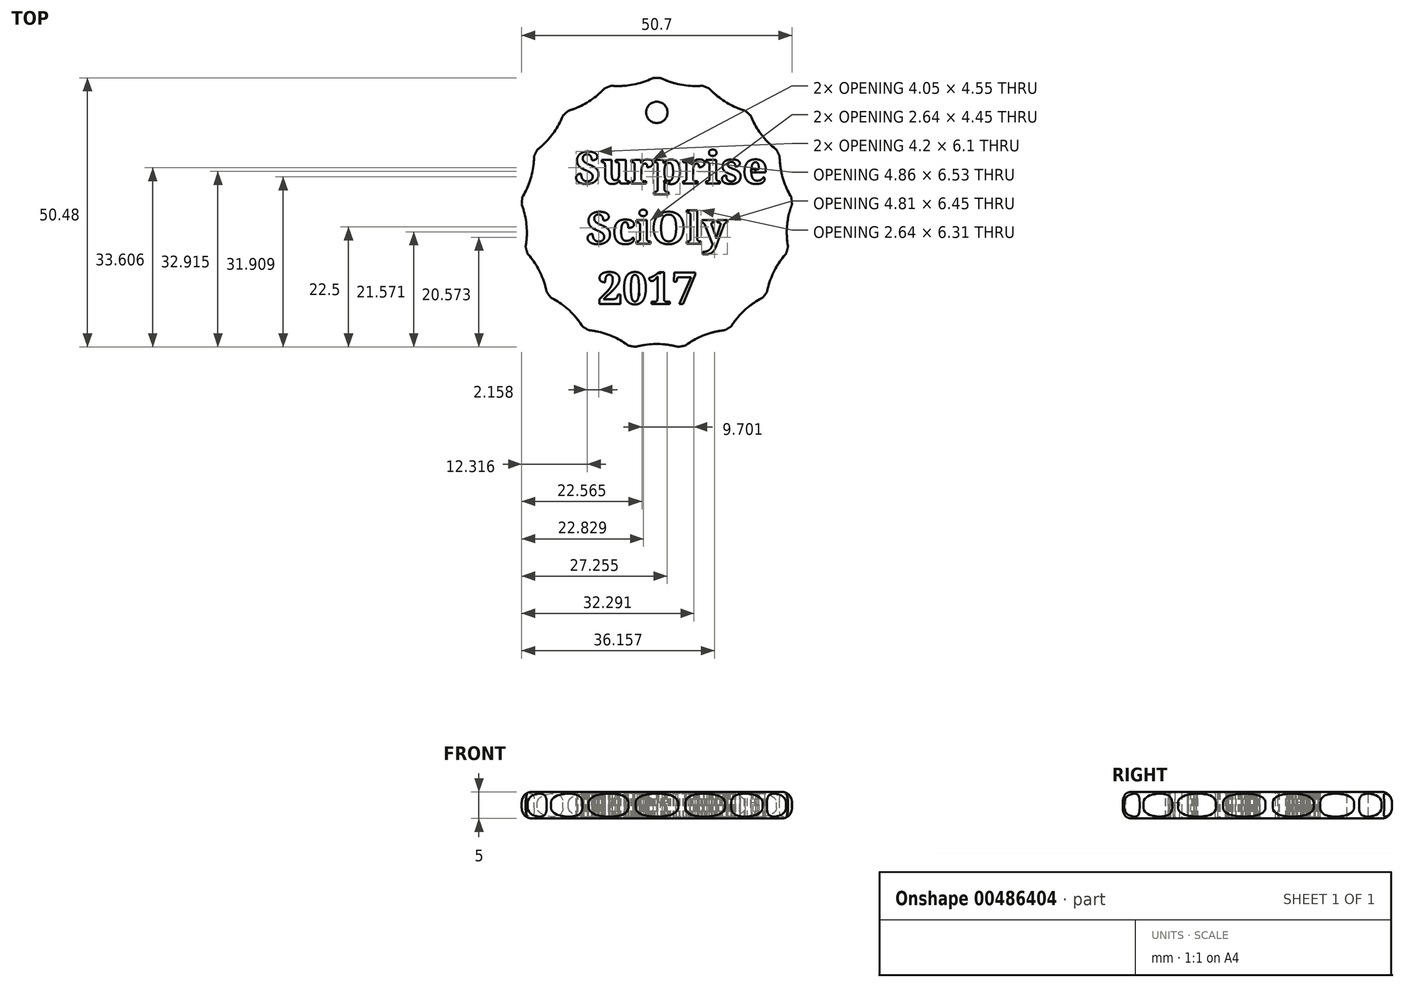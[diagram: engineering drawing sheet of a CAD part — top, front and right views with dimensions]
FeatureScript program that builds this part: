
annotation { "Feature Type Name" : "Feature", "Feature Type Description" : "" }
export const myFeature = defineFeature(function(context is Context, id is Id, definition is map)
    precondition{}
    {
        {
            var Q0;
            Q0=qCreatedBy(makeId("Top.planeOp"),FACE);
            var sketch = newSketch(context, id + "F0", { "sketchPlane" : qUnion([Q0])});
            skCircle(sketch, "E0", {"center": v(0, 0) * mm, "radius": 25.4 * mm});
            skSolve(sketch);
        }
        {
            var Q0;
            Q0=makeQuery(id+"F0.imprint","IMPRINT",FACE,{"disambiguationData":[TD([[makeQuery(id+"F0.imprint","IMPRINT",EDGE,{"derivedFrom":sQuery(id+"F0.wireOp",EDGE,"E0")}),1.0]])]});
            extrude(context, id + "F1", {"entities" : qUnion([Q0]), "depth" : 5 * mm});
        }
        {
            var Q0;
            Q0=makeQuery(id+"F1.opExtrude","CAP_EDGE",EDGE,{"disambiguationData":[OSD([sQuery(id+"F0.wireOp",EDGE,"E0")])],"isStart":false});
            var Q1;
            Q1=makeQuery(id+"F1.opExtrude","CAP_EDGE",EDGE,{"disambiguationData":[OSD([sQuery(id+"F0.wireOp",EDGE,"E0")])],"isStart":true});
            fillet(context, id + "F2", {"entities" : qUnion([Q0, Q1]), "radius" : 2 * mm, "tangentPropagation" : true, "allowEdgeOverflow" : false});
        }
        {
            var Q0;
            Q0=makeQuery(id+"F1.opExtrude","CAP_FACE",FACE,{"disambiguationData":[OSD([sQuery(id+"F0.wireOp",EDGE,"E0")])],"isStart":false});
            var sketch = newSketch(context, id + "F3", { "sketchPlane" : qUnion([Q0])});
            skText(sketch, "E1", { "text": "  Surprise \n   SciOly\n    2017", "fontName": "NotoSerif-Bold.ttf"});
            const initialGuessF3  = {"E1": [-0.0197, 0.00556, 1, 0, 0.00598]};
            skSetInitialGuess(sketch, initialGuessF3);
            skSolve(sketch);
        }
        {
            var Q0;
            Q0=qSketchRegion(id+"F3",true);
            extrude(context, id + "F4", {"entities" : qUnion([Q0]), "operationType" : NewBodyOperationType.REMOVE, "endBound" : BoundingType.THROUGH_ALL, "oppositeDirection" : true, "depth" : 25.4 * mm});
        }
        {
            var Q0;
            Q0=makeQuery(id+"F4.boolean.opBoolean","SPLIT",FACE,{"disambiguationData":[TD([makeQuery(id+"F4.opExtrude","SWEPT_FACE",FACE,{"disambiguationData":[OSD([sQuery(id+"F3.wireOp",EDGE,"E1.sketch_text.stroke-181")])]})])],"derivedFrom":makeQuery(id+"F1.opExtrude","CAP_FACE",FACE,{"disambiguationData":[OSD([sQuery(id+"F0.wireOp",EDGE,"E0")])],"isStart":true})});
            var sketch = newSketch(context, id + "F5", { "sketchPlane" : qUnion([Q0])});
            skLineSegment(sketch, "E2.bottom", {"start": v(2.38, -6.07) * mm, "end": v(1.58, -6.07) * mm});
            skLineSegment(sketch, "E2.top", {"start": v(2.38, -4.55) * mm, "end": v(1.58, -4.55) * mm});
            skLineSegment(sketch, "E2.left", {"start": v(2.38, -6.07) * mm, "end": v(2.38, -4.55) * mm});
            skLineSegment(sketch, "E2.right", {"start": v(1.58, -6.07) * mm, "end": v(1.58, -4.55) * mm});
            skSolve(sketch);
        }
        {
            var Q0;
            Q0=qSketchRegion(id+"F5",true);
            extrude(context, id + "F6", {"entities" : qUnion([Q0]), "operationType" : NewBodyOperationType.ADD, "oppositeDirection" : true, "depth" : 3 * mm});
        }
        {
            var Q0;
            {var subQ0=sQuery(id+"F0.wireOp",EDGE,"E0");var subQ1=makeQuery(id+"F1.opExtrude","CAP_FACE",FACE,{"disambiguationData":[OSD([subQ0])],"isStart":true});Q0=makeQuery(id+"F6.boolean.opBoolean","MERGE",FACE,{"derivedFrom":[makeQuery(id+"F4.boolean.opBoolean","SPLIT",FACE,{"disambiguationData":[TD([makeQuery(id+"F4.opExtrude","SWEPT_FACE",FACE,{"disambiguationData":[OSD([sQuery(id+"F3.wireOp",EDGE,"E1.sketch_text.stroke-181")])]})])],"derivedFrom":subQ1}),makeQuery(id+"F4.boolean.opBoolean","SPLIT",FACE,{"disambiguationData":[TD([makeQuery(id+"F4.opExtrude","SWEPT_FACE",FACE,{"disambiguationData":[OSD([sQuery(id+"F3.wireOp",EDGE,"E1.sketch_text.stroke-0")])]})])],"derivedFrom":subQ1}),makeQuery(id+"F6.opExtrude","CAP_FACE",FACE,{"disambiguationData":[OSD([sQuery(id+"F5.wireOp",EDGE,"E2.bottom"),sQuery(id+"F5.wireOp",EDGE,"E2.top"),sQuery(id+"F5.wireOp",EDGE,"E2.left"),sQuery(id+"F5.wireOp",EDGE,"E2.right")])],"isStart":true})]});}
            var sketch = newSketch(context, id + "F7", { "sketchPlane" : qUnion([Q0])});
            skLineSegment(sketch, "E3.bottom", {"start": v(17.7, -8.23) * mm, "end": v(18.5, -8.23) * mm});
            skLineSegment(sketch, "E3.top", {"start": v(17.7, -7.7) * mm, "end": v(18.5, -7.7) * mm});
            skLineSegment(sketch, "E3.left", {"start": v(17.7, -8.23) * mm, "end": v(17.7, -7.7) * mm});
            skLineSegment(sketch, "E3.right", {"start": v(18.5, -8.23) * mm, "end": v(18.5, -7.7) * mm});
            skSolve(sketch);
        }
        {
            var Q0;
            Q0=makeQuery(id+"F7.imprint","IMPRINT",FACE,{"disambiguationData":[TD([[makeQuery(id+"F7.imprint","IMPRINT",EDGE,{"derivedFrom":sQuery(id+"F7.wireOp",EDGE,"E3.bottom")}),1.0]])]});
            extrude(context, id + "F8", {"entities" : qUnion([Q0]), "operationType" : NewBodyOperationType.ADD, "oppositeDirection" : true, "depth" : 3 * mm});
        }
        {
            var Q0;
            {var subQ0=sQuery(id+"F0.wireOp",EDGE,"E0");var subQ1=makeQuery(id+"F1.opExtrude","CAP_FACE",FACE,{"disambiguationData":[OSD([subQ0])],"isStart":true});Q0=makeQuery(id+"F8.boolean.opBoolean","MERGE",FACE,{"derivedFrom":[makeQuery(id+"F4.boolean.opBoolean","SPLIT",FACE,{"disambiguationData":[TD([makeQuery(id+"F4.opExtrude","SWEPT_FACE",FACE,{"disambiguationData":[OSD([sQuery(id+"F3.wireOp",EDGE,"E1.sketch_text.stroke-325")])]})])],"derivedFrom":subQ1}),makeQuery(id+"F6.boolean.opBoolean","MERGE",FACE,{"derivedFrom":[makeQuery(id+"F4.boolean.opBoolean","SPLIT",FACE,{"disambiguationData":[TD([makeQuery(id+"F4.opExtrude","SWEPT_FACE",FACE,{"disambiguationData":[OSD([sQuery(id+"F3.wireOp",EDGE,"E1.sketch_text.stroke-181")])]})])],"derivedFrom":subQ1}),makeQuery(id+"F4.boolean.opBoolean","SPLIT",FACE,{"disambiguationData":[TD([makeQuery(id+"F4.opExtrude","SWEPT_FACE",FACE,{"disambiguationData":[OSD([sQuery(id+"F3.wireOp",EDGE,"E1.sketch_text.stroke-0")])]})])],"derivedFrom":subQ1}),makeQuery(id+"F6.opExtrude","CAP_FACE",FACE,{"disambiguationData":[OSD([sQuery(id+"F5.wireOp",EDGE,"E2.bottom"),sQuery(id+"F5.wireOp",EDGE,"E2.top"),sQuery(id+"F5.wireOp",EDGE,"E2.left"),sQuery(id+"F5.wireOp",EDGE,"E2.right")])],"isStart":true})]}),makeQuery(id+"F8.opExtrude","CAP_FACE",FACE,{"disambiguationData":[OSD([sQuery(id+"F7.wireOp",EDGE,"E3.bottom"),sQuery(id+"F7.wireOp",EDGE,"E3.top"),sQuery(id+"F7.wireOp",EDGE,"E3.left"),sQuery(id+"F7.wireOp",EDGE,"E3.right")])],"isStart":true})]});}
            var sketch = newSketch(context, id + "F9", { "sketchPlane" : qUnion([Q0])});
            skLineSegment(sketch, "E4.bottom", {"start": v(-13.45, 0.6) * mm, "end": v(-14.25, 0.6) * mm});
            skLineSegment(sketch, "E4.top", {"start": v(-13.45, 1.32) * mm, "end": v(-14.25, 1.32) * mm});
            skLineSegment(sketch, "E4.left", {"start": v(-13.45, 0.6) * mm, "end": v(-13.45, 1.32) * mm});
            skLineSegment(sketch, "E4.right", {"start": v(-14.25, 0.6) * mm, "end": v(-14.25, 1.32) * mm});
            skSolve(sketch);
        }
        {
            var Q0;
            {var subQ0=sQuery(id+"F9.wireOp",EDGE,"E4.bottom");Q0=makeQuery(id+"F9.imprint","IMPRINT",FACE,{"disambiguationData":[TD([[makeQuery(id+"F9.imprint","IMPRINT",EDGE,{"derivedFrom":subQ0}),-1.0]])]});}
            var Q1;
            {var subQ0=sQuery(id+"F9.wireOp",EDGE,"E4.top");Q1=makeQuery(id+"F9.imprint","IMPRINT",FACE,{"disambiguationData":[TD([[makeQuery(id+"F9.imprint","IMPRINT",EDGE,{"derivedFrom":subQ0}),1.0]])]});}
            extrude(context, id + "F10", {"entities" : qUnion([Q0, Q1]), "operationType" : NewBodyOperationType.ADD, "oppositeDirection" : true, "depth" : 3 * mm});
        }
        {
            var Q0;
            {var subQ0=sQuery(id+"F0.wireOp",EDGE,"E0");var subQ1=makeQuery(id+"F1.opExtrude","CAP_FACE",FACE,{"disambiguationData":[OSD([subQ0])],"isStart":true});Q0=makeQuery(id+"F10.boolean.opBoolean","MERGE",FACE,{"derivedFrom":[makeQuery(id+"F4.boolean.opBoolean","SPLIT",FACE,{"disambiguationData":[TD([makeQuery(id+"F4.opExtrude","SWEPT_FACE",FACE,{"disambiguationData":[OSD([sQuery(id+"F3.wireOp",EDGE,"E1.sketch_text.stroke-404")])]})])],"derivedFrom":subQ1}),makeQuery(id+"F8.boolean.opBoolean","MERGE",FACE,{"derivedFrom":[makeQuery(id+"F4.boolean.opBoolean","SPLIT",FACE,{"disambiguationData":[TD([makeQuery(id+"F4.opExtrude","SWEPT_FACE",FACE,{"disambiguationData":[OSD([sQuery(id+"F3.wireOp",EDGE,"E1.sketch_text.stroke-325")])]})])],"derivedFrom":subQ1}),makeQuery(id+"F6.boolean.opBoolean","MERGE",FACE,{"derivedFrom":[makeQuery(id+"F4.boolean.opBoolean","SPLIT",FACE,{"disambiguationData":[TD([makeQuery(id+"F4.opExtrude","SWEPT_FACE",FACE,{"disambiguationData":[OSD([sQuery(id+"F3.wireOp",EDGE,"E1.sketch_text.stroke-181")])]})])],"derivedFrom":subQ1}),makeQuery(id+"F4.boolean.opBoolean","SPLIT",FACE,{"disambiguationData":[TD([makeQuery(id+"F4.opExtrude","SWEPT_FACE",FACE,{"disambiguationData":[OSD([sQuery(id+"F3.wireOp",EDGE,"E1.sketch_text.stroke-0")])]})])],"derivedFrom":subQ1}),makeQuery(id+"F6.opExtrude","CAP_FACE",FACE,{"disambiguationData":[OSD([sQuery(id+"F5.wireOp",EDGE,"E2.bottom"),sQuery(id+"F5.wireOp",EDGE,"E2.top"),sQuery(id+"F5.wireOp",EDGE,"E2.left"),sQuery(id+"F5.wireOp",EDGE,"E2.right")])],"isStart":true})]}),makeQuery(id+"F8.opExtrude","CAP_FACE",FACE,{"disambiguationData":[OSD([sQuery(id+"F7.wireOp",EDGE,"E3.bottom"),sQuery(id+"F7.wireOp",EDGE,"E3.top"),sQuery(id+"F7.wireOp",EDGE,"E3.left"),sQuery(id+"F7.wireOp",EDGE,"E3.right")])],"isStart":true})]}),makeQuery(id+"F10.opExtrude","CAP_FACE",FACE,{"disambiguationData":[OSD([sQuery(id+"F9.wireOp",EDGE,"E4.bottom"),sQuery(id+"F9.wireOp",EDGE,"E4.top"),sQuery(id+"F9.wireOp",EDGE,"E4.left"),sQuery(id+"F9.wireOp",EDGE,"E4.right")])],"isStart":true})]});}
            var sketch = newSketch(context, id + "F11", { "sketchPlane" : qUnion([Q0])});
            skLineSegment(sketch, "E5.bottom", {"start": v(0.76, 10.49) * mm, "end": v(-1.62, 10.49) * mm});
            skLineSegment(sketch, "E5.top", {"start": v(0.76, 11.29) * mm, "end": v(-1.62, 11.29) * mm});
            skLineSegment(sketch, "E5.left", {"start": v(0.76, 10.49) * mm, "end": v(0.76, 11.29) * mm});
            skLineSegment(sketch, "E5.right", {"start": v(-1.62, 10.49) * mm, "end": v(-1.62, 11.29) * mm});
            skSolve(sketch);
        }
        {
            var Q0;
            Q0=qSketchRegion(id+"F11",true);
            extrude(context, id + "F12", {"entities" : qUnion([Q0]), "operationType" : NewBodyOperationType.ADD, "oppositeDirection" : true, "depth" : 3 * mm});
        }
        {
            var Q0;
            {var subQ0=sQuery(id+"F0.wireOp",EDGE,"E0");var subQ1=makeQuery(id+"F1.opExtrude","CAP_FACE",FACE,{"disambiguationData":[OSD([subQ0])],"isStart":true});Q0=makeQuery(id+"F12.boolean.opBoolean","MERGE",FACE,{"derivedFrom":[makeQuery(id+"F4.boolean.opBoolean","SPLIT",FACE,{"disambiguationData":[TD([makeQuery(id+"F4.opExtrude","SWEPT_FACE",FACE,{"disambiguationData":[OSD([sQuery(id+"F3.wireOp",EDGE,"E1.sketch_text.stroke-834")])]})])],"derivedFrom":subQ1}),makeQuery(id+"F10.boolean.opBoolean","MERGE",FACE,{"derivedFrom":[makeQuery(id+"F4.boolean.opBoolean","SPLIT",FACE,{"disambiguationData":[TD([makeQuery(id+"F4.opExtrude","SWEPT_FACE",FACE,{"disambiguationData":[OSD([sQuery(id+"F3.wireOp",EDGE,"E1.sketch_text.stroke-404")])]})])],"derivedFrom":subQ1}),makeQuery(id+"F8.boolean.opBoolean","MERGE",FACE,{"derivedFrom":[makeQuery(id+"F4.boolean.opBoolean","SPLIT",FACE,{"disambiguationData":[TD([makeQuery(id+"F4.opExtrude","SWEPT_FACE",FACE,{"disambiguationData":[OSD([sQuery(id+"F3.wireOp",EDGE,"E1.sketch_text.stroke-325")])]})])],"derivedFrom":subQ1}),makeQuery(id+"F6.boolean.opBoolean","MERGE",FACE,{"derivedFrom":[makeQuery(id+"F4.boolean.opBoolean","SPLIT",FACE,{"disambiguationData":[TD([makeQuery(id+"F4.opExtrude","SWEPT_FACE",FACE,{"disambiguationData":[OSD([sQuery(id+"F3.wireOp",EDGE,"E1.sketch_text.stroke-181")])]})])],"derivedFrom":subQ1}),makeQuery(id+"F4.boolean.opBoolean","SPLIT",FACE,{"disambiguationData":[TD([makeQuery(id+"F4.opExtrude","SWEPT_FACE",FACE,{"disambiguationData":[OSD([sQuery(id+"F3.wireOp",EDGE,"E1.sketch_text.stroke-0")])]})])],"derivedFrom":subQ1}),makeQuery(id+"F6.opExtrude","CAP_FACE",FACE,{"disambiguationData":[OSD([sQuery(id+"F5.wireOp",EDGE,"E2.bottom"),sQuery(id+"F5.wireOp",EDGE,"E2.top"),sQuery(id+"F5.wireOp",EDGE,"E2.left"),sQuery(id+"F5.wireOp",EDGE,"E2.right")])],"isStart":true})]}),makeQuery(id+"F8.opExtrude","CAP_FACE",FACE,{"disambiguationData":[OSD([sQuery(id+"F7.wireOp",EDGE,"E3.bottom"),sQuery(id+"F7.wireOp",EDGE,"E3.top"),sQuery(id+"F7.wireOp",EDGE,"E3.left"),sQuery(id+"F7.wireOp",EDGE,"E3.right")])],"isStart":true})]}),makeQuery(id+"F10.opExtrude","CAP_FACE",FACE,{"disambiguationData":[OSD([sQuery(id+"F9.wireOp",EDGE,"E4.bottom"),sQuery(id+"F9.wireOp",EDGE,"E4.top"),sQuery(id+"F9.wireOp",EDGE,"E4.left"),sQuery(id+"F9.wireOp",EDGE,"E4.right")])],"isStart":true})]}),makeQuery(id+"F12.opExtrude","CAP_FACE",FACE,{"disambiguationData":[OSD([sQuery(id+"F11.wireOp",EDGE,"E5.bottom"),sQuery(id+"F11.wireOp",EDGE,"E5.top"),sQuery(id+"F11.wireOp",EDGE,"E5.left"),sQuery(id+"F11.wireOp",EDGE,"E5.right")])],"isStart":true})]});}
            var sketch = newSketch(context, id + "F13", { "sketchPlane" : qUnion([Q0])});
            skLineSegment(sketch, "E6", {"start": v(-3.3, 15.52) * mm, "end": v(-3.37, 14.04) * mm});
            skLineSegment(sketch, "E7", {"start": v(-3.37, 14.04) * mm, "end": v(-4.15, 14.6) * mm});
            skLineSegment(sketch, "E8", {"start": v(-4.15, 14.6) * mm, "end": v(-4.07, 16.28) * mm});
            skLineSegment(sketch, "E9", {"start": v(-4.07, 16.28) * mm, "end": v(-3.3, 15.52) * mm});
            skSolve(sketch);
        }
        {
            var Q0;
            {var subQ1=sQuery(id+"F13.wireOp",EDGE,"E9");Q0=makeQuery(id+"F13.imprint","IMPRINT",FACE,{"disambiguationData":[TD([[makeQuery(id+"F13.imprint","IMPRINT",EDGE,{"derivedFrom":subQ1}),-1.0]])]});}
            var Q1;
            Q1=makeQuery(id+"F13.imprint","IMPRINT",FACE,{"disambiguationData":[TD([[makeQuery(id+"F13.imprint","IMPRINT",EDGE,{"derivedFrom":sQuery(id+"F13.wireOp",EDGE,"E6")}),-1.0]])]});
            extrude(context, id + "F14", {"entities" : qUnion([Q0, Q1]), "operationType" : NewBodyOperationType.ADD, "oppositeDirection" : true, "depth" : 3 * mm});
        }
        {
            var Q0;
            {var subQ0=sQuery(id+"F0.wireOp",EDGE,"E0");Q0=makeQuery(id+"F4.boolean.opBoolean","SPLIT",FACE,{"disambiguationData":[TD([makeQuery(id+"F4.opExtrude","SWEPT_FACE",FACE,{"disambiguationData":[OSD([sQuery(id+"F3.wireOp",EDGE,"E1.sketch_text.stroke-0")])]})])],"derivedFrom":makeQuery(id+"F1.opExtrude","CAP_FACE",FACE,{"disambiguationData":[OSD([subQ0])],"isStart":false})});}
            var sketch = newSketch(context, id + "F15", { "sketchPlane" : qUnion([Q0])});
            skCircle(sketch, "E10", {"center": v(0, 18.93) * mm, "radius": 2 * mm});
            skSolve(sketch);
        }
        {
            var Q0;
            Q0=qSketchRegion(id+"F15",true);
            extrude(context, id + "F16", {"entities" : qUnion([Q0]), "operationType" : NewBodyOperationType.REMOVE, "endBound" : BoundingType.THROUGH_ALL, "oppositeDirection" : true, "depth" : 25 * mm});
        }
        {
            var Q0;
            {var subQ0=sQuery(id+"F0.wireOp",EDGE,"E0");Q0=makeQuery(id+"F2.opFillet","BLEND_FACE",FACE,{"disambiguationData":[OSD([subQ0]),TDD([makeQuery(id+"F1.opExtrude","CAP_EDGE",EDGE,{"disambiguationData":[OSD([subQ0])],"isStart":true})])]});}
            var Q1;
            Q1=makeQuery(id+"F16.boolean.opBoolean","COPY",EDGE,{"derivedFrom":makeQuery(id+"F16.opExtrude","CAP_EDGE",EDGE,{"disambiguationData":[OSD([sQuery(id+"F15.wireOp",EDGE,"E10")])],"isStart":true})});
            var Q2;
            Q2=makeQuery(id+"F16.boolean.opBoolean","COPY",FACE,{"derivedFrom":makeQuery(id+"F16.opExtrude","SWEPT_FACE",FACE,{"disambiguationData":[OSD([sQuery(id+"F15.wireOp",EDGE,"E10")])]})});
            fillet(context, id + "F17", {"entities" : qUnion([Q0, Q1, Q2]), "radius" : .6 * mm, "tangentPropagation" : true, "allowEdgeOverflow" : false});
        }
        {
            var Q0;
            {var subQ0=sQuery(id+"F0.wireOp",EDGE,"E0");Q0=makeQuery(id+"F4.boolean.opBoolean","SPLIT",FACE,{"disambiguationData":[TD([makeQuery(id+"F4.opExtrude","SWEPT_FACE",FACE,{"disambiguationData":[OSD([sQuery(id+"F3.wireOp",EDGE,"E1.sketch_text.stroke-0")])]})])],"derivedFrom":makeQuery(id+"F1.opExtrude","CAP_FACE",FACE,{"disambiguationData":[OSD([subQ0])],"isStart":false})});}
            var sketch = newSketch(context, id + "F18", { "sketchPlane" : qUnion([Q0])});
            skArc(sketch, "E11", {"start": v(0.68, 25.4) * mm, "mid": v(4.5, 24.12) * mm, "end": v(8.54, 23.92) * mm});
            skPoint(sketch, "E11.first.point", {"position": v(0.68, 25.4) * mm});
            skPoint(sketch, "E11.second.point", {"position": v(8.54, 23.92) * mm});
            skArc(sketch, "E12.0", {"start": v(8.54, 23.92) * mm, "mid": v(4.67, 24.97) * mm, "end": v(0.68, 25.4) * mm});
            skSolve(sketch);
        }
        {
            var Q0;
            Q0=qSketchRegion(id+"F18",true);
            extrude(context, id + "F19", {"entities" : qUnion([Q0]), "operationType" : NewBodyOperationType.REMOVE, "endBound" : BoundingType.THROUGH_ALL, "oppositeDirection" : true, "depth" : 25 * mm});
        }
        {
            var Q0;
            Q0=makeQuery(id+"F19.boolean.opBoolean","COPY",FACE,{"derivedFrom":makeQuery(id+"F19.opExtrude","SWEPT_FACE",FACE,{"disambiguationData":[OSD([sQuery(id+"F18.wireOp",EDGE,"E11")])]})});
            var Q1;
            {var subQ0=sQuery(id+"F0.wireOp",EDGE,"E0");Q1=makeQuery(id+"F2.opFillet","BLEND_EDGE",EDGE,{"blendedFrom":[makeQuery(id+"F1.opExtrude","CAP_EDGE",EDGE,{"disambiguationData":[OSD([subQ0])],"isStart":false}),makeQuery(id+"F1.opExtrude","CAP_FACE",FACE,{"disambiguationData":[OSD([subQ0])],"isStart":false})],"blendedInto":[makeQuery(id+"F1.opExtrude","CAP_FACE",FACE,{"disambiguationData":[OSD([subQ0])],"isStart":false})]});}
            circularPattern(context, id + "F20", {"patternType" : PatternType.FACE, "operationType" : NewBodyOperationType.REMOVE, "faces" : qUnion([Q0]), "axis" : qUnion([Q1]), "angle" : 360 * degree, "instanceCount" : 17, "equalSpace" : true});
        }
    });
